# Revit family: Kaskad-Double_Planter-9x36-Magnusongroup-1
name_source: partatom
category: Furniture
revit_build: Autodesk Revit 2016 (Build: 20150220_1215(x64)
units: mm (PartAtom-declared; Revit-internal decimal feet)

## family parameters
Always vertical = Yes
Cut with Voids When Loaded = No
Room Calculation Point = No
Shared = No
Work Plane-Based = No

## types (3) — shared parameters
Assembly Code = E2020200
Depth = 36"
Frame = Steel, Wrought
Glides = UHMW, Black
Heigth Plants = 12"
Keynote = 12500
Liner = UHMW, Black
Manufacturer = MAGNUSON GROUP
Type Comments = KASKAD
URL = www.magnusongroup.com
Width = 9"

## per-type parameters (varying)
| type | Cost | Description | Height |
| KAS-0936H | 985 $ | Painted steel 9" x 36" double rectangular planter with liner and adjustable glides 36" Height | 36" |
| KAS-0936M | 855 $ | Painted steel 9" x 36" double rectangular planter with liner and adjustable glides 20" Height | 20" |
| KAS-0936S | 725 $ | Painted steel 9" x 36" double rectangular planter with liner and adjustable glides 12" Height | 12" |

note: column(s) folded — value = type name in every type: Model

## geometry (parser evidence)
native form markers: Sweep x4
no freeform markers — native parametric forms only
